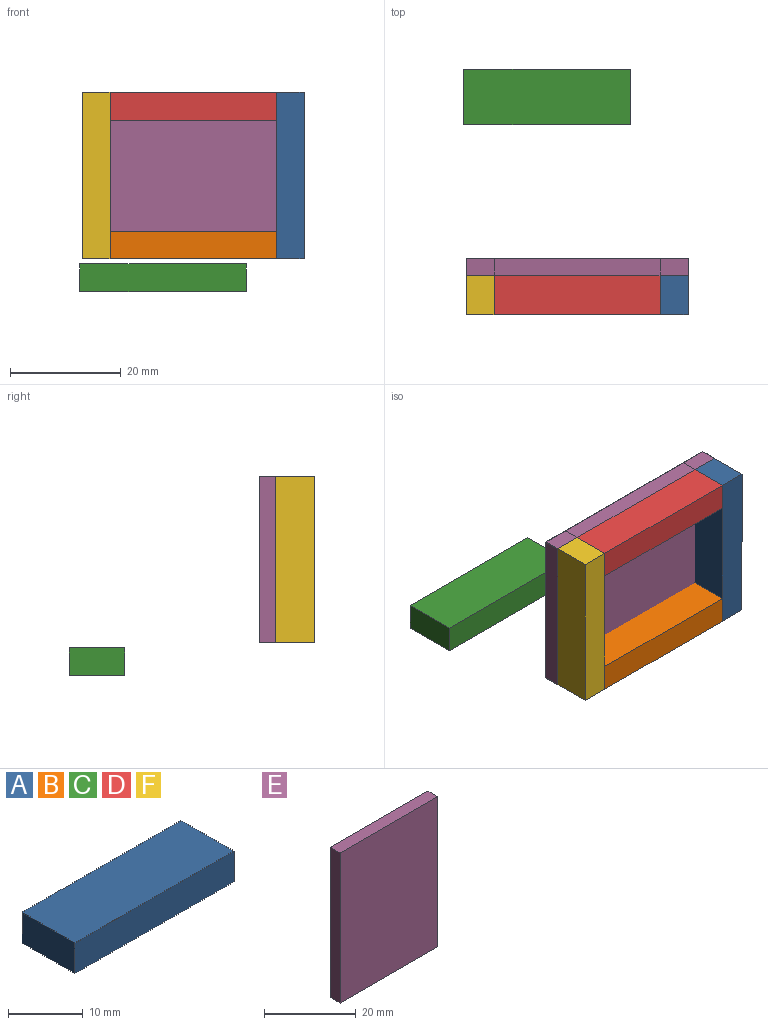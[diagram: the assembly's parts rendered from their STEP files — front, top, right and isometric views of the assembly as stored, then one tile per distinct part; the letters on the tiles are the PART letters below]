
ASSEMBLY  parts=6 mates=4
PART A: 6 faces, bbox 30x10x5 mm
  f0: plane 30x10mm, normal (0,0,1), area 300mm2, adj f1,f3,f4,f5
  f1: plane 10x5mm, normal (-1,0,0), area 50mm2, adj f0,f2,f4,f5
  f2: plane 30x10mm, normal (0,0,-1), area 300mm2, adj f1,f3,f4,f5
  f3: plane 10x5mm, normal (1,0,0), area 50mm2, adj f0,f2,f4,f5
  f4: plane 30x5mm, normal (0,-1,0), area 150mm2, adj f0,f1,f2,f3
  f5: plane 30x5mm, normal (0,1,0), area 150mm2, adj f0,f1,f2,f3
PART B: same geometry as A
PART C: same geometry as A
PART D: same geometry as A
PART E: 6 faces, bbox 30x3x40 mm
  f0: plane 30x3mm, normal (0,0,1), area 90mm2, adj f1,f3,f4,f5
  f1: plane 40x3mm, normal (-1,0,0), area 120mm2, adj f0,f2,f4,f5
  f2: plane 30x3mm, normal (0,0,-1), area 90mm2, adj f1,f3,f4,f5
  f3: plane 40x3mm, normal (1,0,0), area 120mm2, adj f0,f2,f4,f5
  f4: plane 40x30mm, normal (0,-1,0), area 1200mm2, adj f0,f1,f2,f3
  f5: plane 40x30mm, normal (0,1,0), area 1200mm2, adj f0,f1,f2,f3
PART F: same geometry as A
PLACE A rot(axis=(0,-1,0),90deg) t=(27.52,-34.23,104.29)mm
PLACE B t=(26.53,-34.23,16.34)mm
PLACE C t=(21.1,0,10.42)mm
PLACE D t=(26.53,-34.23,41.34)mm
PLACE E rot(axis=(0.71,0,0.71),180deg) t=(-51.93,-37.23,95.01)mm
PLACE F rot(axis=(0,1,0),90deg) t=(-66.42,-34.23,12.32)mm
MATE fastened A.f0 <-> B.f3  axis (-1,0,0) through (-4.45,-39.23,43.31)mm
MATE fastened F.f0 <-> D.f1  axis (1,0,0) through (-34.45,-39.23,73.31)mm
MATE fastened E.f4 <-> A.f5  axis (0,1,0) through (0.55,-34.23,58.31)mm
MATE fastened F.f0 <-> B.f1  axis (1,0,0) through (-34.45,-39.23,43.31)mm
